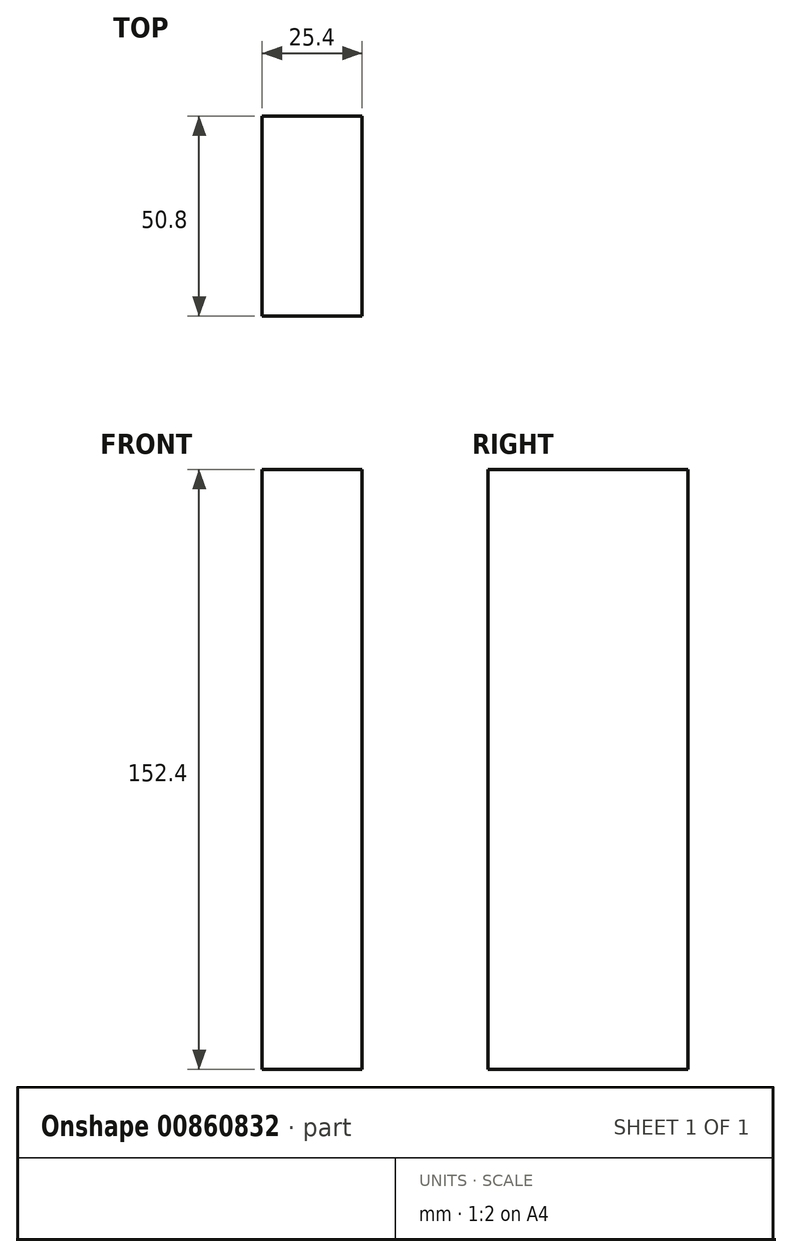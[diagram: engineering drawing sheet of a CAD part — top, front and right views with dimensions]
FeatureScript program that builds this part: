
annotation { "Feature Type Name" : "Feature", "Feature Type Description" : "" }
export const myFeature = defineFeature(function(context is Context, id is Id, definition is map)
    precondition{}
    {
        {
            var Q0;
            Q0=qCreatedBy(makeId("Front.planeOp"),FACE);
            var sketch = newSketch(context, id + "F0", { "sketchPlane" : qUnion([Q0])});
            skLineSegment(sketch, "E0.bottom", {"start": v(-61.11, 75.92) * mm, "end": v(-35.71, 75.92) * mm});
            skLineSegment(sketch, "E0.top", {"start": v(-61.11, -76.48) * mm, "end": v(-35.71, -76.48) * mm});
            skLineSegment(sketch, "E0.left", {"start": v(-61.11, 75.92) * mm, "end": v(-61.11, -76.48) * mm});
            skLineSegment(sketch, "E0.right", {"start": v(-35.71, 75.92) * mm, "end": v(-35.71, -76.48) * mm});
            skSolve(sketch);
        }
        {
            var Q0;
            Q0 = qSketchRegion(id + "F0", true);
            extrude(context, id + "F1", {"entities" : qUnion([Q0]), "depth" : 50.8 * mm, "offsetDistance" : 25.4 * mm});
        }
    });
